# Revit family: WLV_A3-2000x2600-Louvre
name_source: partatom
category: Windows
revit_build: Autodesk Revit 2016 (Build: 20150220_1215(x64)
units: mm (PartAtom-declared; Revit-internal decimal feet)

## family parameters
Always vertical = Yes
Cut with Voids When Loaded = No
Host = Wall
Room Calculation Point = No
Shared = No

## types (1)
- 1190 x 1190 Louvre
    Array = 11
    Default Sill Height = 800 mm  [stored 2.62467 ft]
    Frame Finish = Default Frame
    Frame Width = 50 mm  [stored 0.164042 ft]
    Head Height = 2125 mm  [stored 6.97178 ft]
    Height = 1190 mm  [stored 3.9042 ft]
    Inset = 115 mm  [stored 0.377297 ft]
    Inside Height = 1100 mm
    Inside Width = 1100 mm
    Louvre Angle = 15.00°
    Louvre Finish = Default Louvre
    Louvre Width = 100 mm  [stored 0.328084 ft]
    Lovre Height Half = 100 mm  [stored 0.328084 ft]
    Wall Closure = By host
    Width = 1190 mm  [stored 3.9042 ft]

note: [stored X ft] marks values corroborated as IEEE doubles in the binary element streams (Revit-internal decimal feet)

## geometry (parser evidence)
native form markers: Sweep x5
no freeform markers — native parametric forms only
